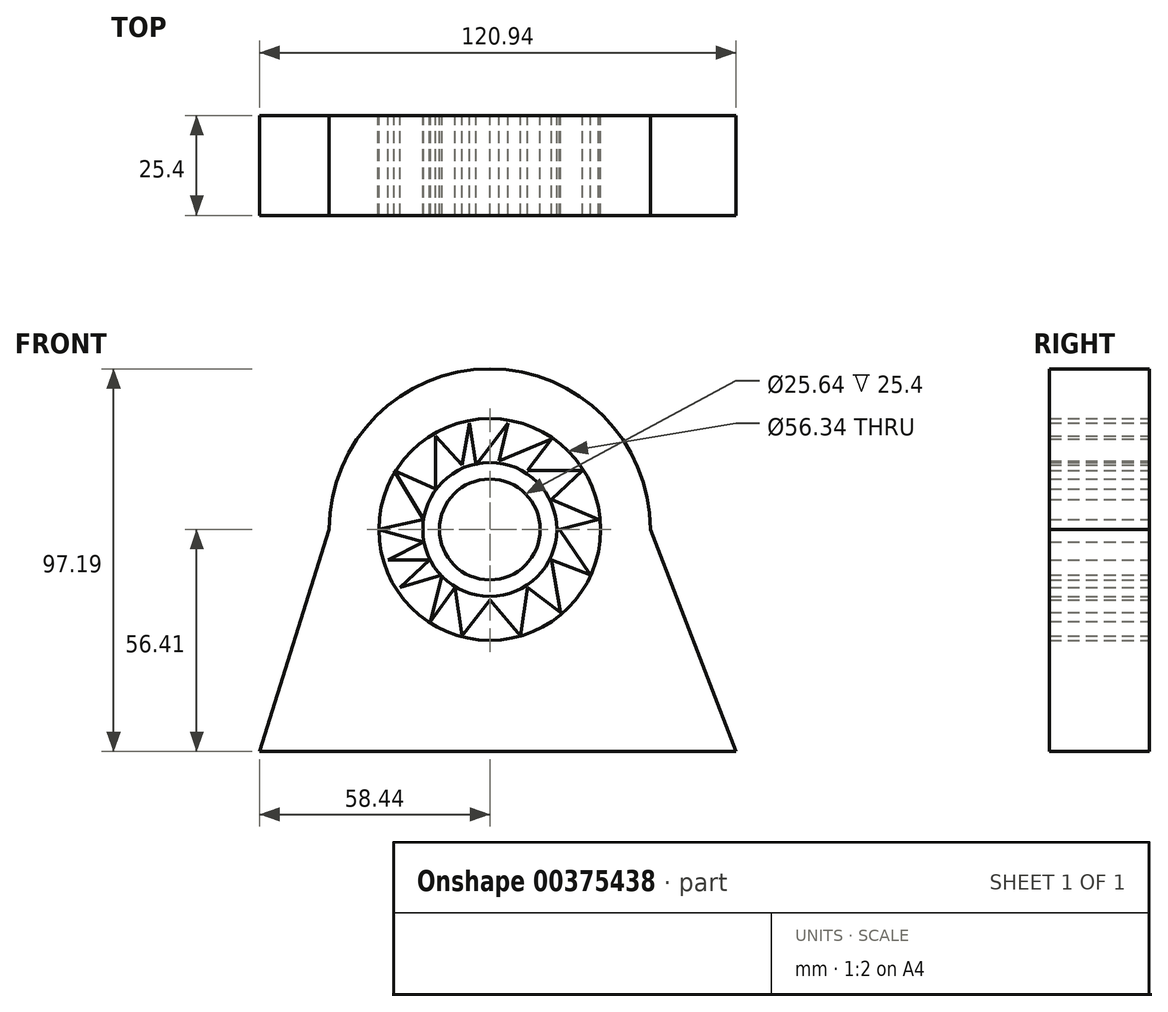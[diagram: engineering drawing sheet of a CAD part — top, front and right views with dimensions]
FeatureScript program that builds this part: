
annotation { "Feature Type Name" : "Feature", "Feature Type Description" : "" }
export const myFeature = defineFeature(function(context is Context, id is Id, definition is map)
    precondition{}
    {
        {
            var Q0;
            Q0=qCreatedBy(makeId("Front.planeOp"),FACE);
            var sketch = newSketch(context, id + "F0", { "sketchPlane" : qUnion([Q0])});
            skCircle(sketch, "E0", {"center": v(0, 0) * mm, "radius": 28.17 * mm});
            skCircle(sketch, "E1", {"center": v(0, 0) * mm, "radius": 40.78 * mm});
            skLineSegment(sketch, "E2", {"start": v(40.78, 0) * mm, "end": v(62.5, -56.41) * mm});
            skLineSegment(sketch, "E3", {"start": v(-40.78, 0) * mm, "end": v(-58.44, -56.41) * mm});
            skLineSegment(sketch, "E4", {"start": v(-58.44, -56.41) * mm, "end": v(62.5, -56.41) * mm});
            skSolve(sketch);
        }
        {
            var Q0;
            Q0 = qSketchRegion(id + "F0", true);
            extrude(context, id + "F1", {"entities" : qUnion([Q0]), "depth" : 25.4 * mm});
        }
        {
            var Q0;
            Q0=qCreatedBy(makeId("Front.planeOp"),FACE);
            var sketch = newSketch(context, id + "F2", { "sketchPlane" : qUnion([Q0])});
            skCircle(sketch, "E5", {"center": v(0, 0) * mm, "radius": 12.82 * mm});
            skCircle(sketch, "E6", {"center": v(0, 0) * mm, "radius": 17.01 * mm});
            skSolve(sketch);
        }
        {
            var Q0;
            Q0 = qSketchRegion(id + "F2", true);
            extrude(context, id + "F3", {"entities" : qUnion([Q0]), "depth" : 25.4 * mm});
        }
        {
            var Q0;
            Q0=qCreatedBy(makeId("Front.planeOp"),FACE);
            var sketch = newSketch(context, id + "F4", { "sketchPlane" : qUnion([Q0])});
            skLineSegment(sketch, "E7", {"start": v(-15.12, -23.41) * mm, "end": v(-8.85, -14.75) * mm});
            skLineSegment(sketch, "E8", {"start": v(-8.85, -14.75) * mm, "end": v(-7, -27.1) * mm});
            skLineSegment(sketch, "E9", {"start": v(-7, -27.1) * mm, "end": v(0, -17.88) * mm});
            skLineSegment(sketch, "E10", {"start": v(0, -17.88) * mm, "end": v(7.74, -27.1) * mm});
            skLineSegment(sketch, "E11", {"start": v(7.74, -27.1) * mm, "end": v(9.59, -14.75) * mm});
            skLineSegment(sketch, "E12", {"start": v(9.59, -14.75) * mm, "end": v(17.93, -21.09) * mm});
            skLineSegment(sketch, "E13", {"start": v(17.93, -21.09) * mm, "end": v(15.67, -7.74) * mm});
            skLineSegment(sketch, "E14", {"start": v(15.67, -7.74) * mm, "end": v(25.63, -11.61) * mm});
            skLineSegment(sketch, "E15", {"start": v(25.63, -11.61) * mm, "end": v(17.7, 0) * mm});
            skLineSegment(sketch, "E16", {"start": v(17.7, 0) * mm, "end": v(27.65, 2.58) * mm});
            skLineSegment(sketch, "E17", {"start": v(27.65, 2.58) * mm, "end": v(15.67, 7.56) * mm});
            skLineSegment(sketch, "E18", {"start": v(15.67, 7.56) * mm, "end": v(23.6, 14.93) * mm});
            skLineSegment(sketch, "E19", {"start": v(23.6, 14.93) * mm, "end": v(9.59, 14.93) * mm});
            skLineSegment(sketch, "E20", {"start": v(9.59, 14.93) * mm, "end": v(15.67, 22.94) * mm});
            skLineSegment(sketch, "E21", {"start": v(15.67, 22.94) * mm, "end": v(2.4, 17.33) * mm});
            skLineSegment(sketch, "E22", {"start": v(2.4, 17.33) * mm, "end": v(4.6, 27.1) * mm});
            skLineSegment(sketch, "E23", {"start": v(4.6, 27.1) * mm, "end": v(-3.51, 16.41) * mm});
            skLineSegment(sketch, "E24", {"start": v(-3.51, 16.41) * mm, "end": v(-5.16, 27.1) * mm});
            skLineSegment(sketch, "E25", {"start": v(-5.16, 27.1) * mm, "end": v(-7, 16.4) * mm});
            skLineSegment(sketch, "E26", {"start": v(-7, 16.4) * mm, "end": v(-13.79, 23.7) * mm});
            skLineSegment(sketch, "E27", {"start": v(-13.79, 23.7) * mm, "end": v(-13.79, 10.32) * mm});
            skLineSegment(sketch, "E28", {"start": v(-13.79, 10.32) * mm, "end": v(-24.33, 14.93) * mm});
            skLineSegment(sketch, "E29", {"start": v(-24.33, 14.93) * mm, "end": v(-16.78, 2.58) * mm});
            skLineSegment(sketch, "E30", {"start": v(-16.78, 2.58) * mm, "end": v(-28.4, 0) * mm});
            skLineSegment(sketch, "E31", {"start": v(-28.4, 0) * mm, "end": v(-16.78, -3.13) * mm});
            skLineSegment(sketch, "E32", {"start": v(-16.78, -3.13) * mm, "end": v(-25.8, -7.74) * mm});
            skLineSegment(sketch, "E33", {"start": v(-25.8, -7.74) * mm, "end": v(-15.3, -7.74) * mm});
            skLineSegment(sketch, "E34", {"start": v(-15.3, -7.74) * mm, "end": v(-22.83, -14.75) * mm});
            skLineSegment(sketch, "E35", {"start": v(-22.83, -14.75) * mm, "end": v(-12.17, -11.61) * mm});
            skLineSegment(sketch, "E36", {"start": v(-12.17, -11.61) * mm, "end": v(-15.12, -23.41) * mm});
            skSolve(sketch);
        }
        {
            var Q0;
            Q0 = qSketchRegion(id + "F4", true);
            extrude(context, id + "F5", {"entities" : qUnion([Q0]), "depth" : 25.4 * mm});
        }
        {
            var Q0;
            Q0 = qSketchRegion(id + "F4", true);
            extrude(context, id + "F6", {"entities" : qUnion([Q0]), "depth" : 25.4 * mm});
        }
    });
